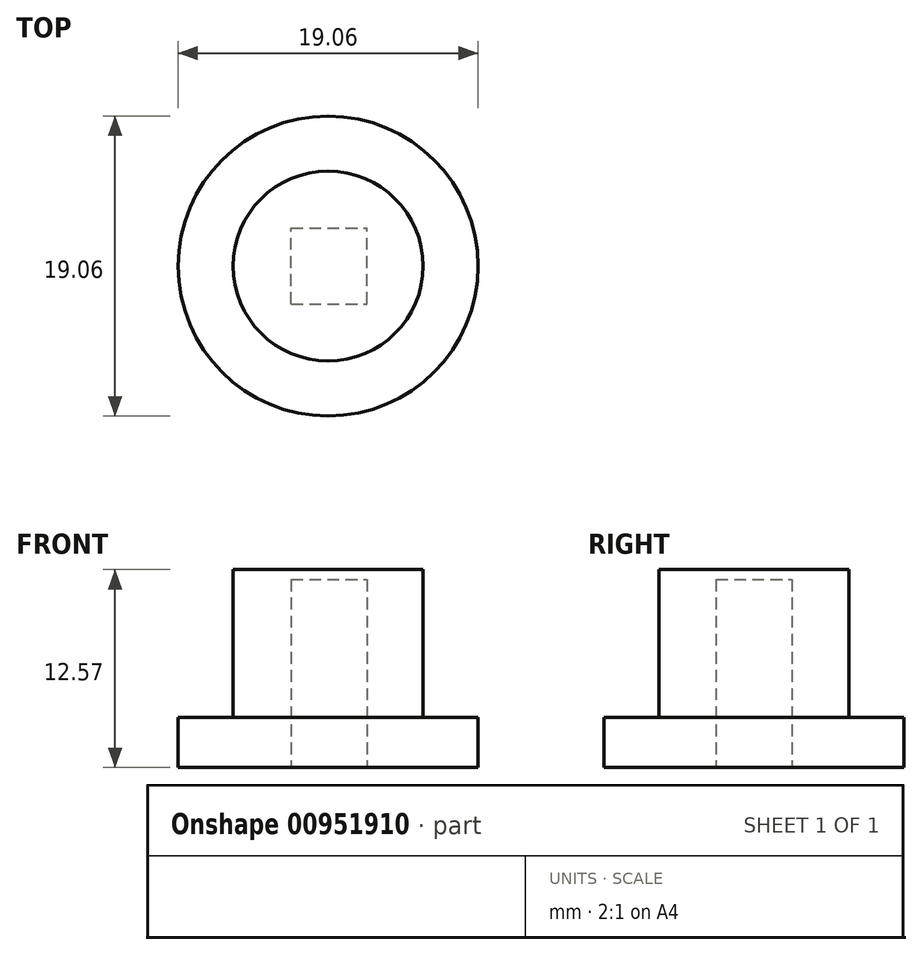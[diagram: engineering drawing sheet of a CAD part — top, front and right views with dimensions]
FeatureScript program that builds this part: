
annotation { "Feature Type Name" : "Feature", "Feature Type Description" : "" }
export const myFeature = defineFeature(function(context is Context, id is Id, definition is map)
    precondition{}
    {
        {
            var Q0;
            Q0=qCreatedBy(makeId("Top.planeOp"),FACE);
            var sketch = newSketch(context, id + "F0", { "sketchPlane" : qUnion([Q0])});
            skCircle(sketch, "E0", {"center": v(0, 0) * mm, "radius": 9.53 * mm});
            skSolve(sketch);
        }
        {
            var Q0;
            Q0=makeQuery(id+"F0.imprint","IMPRINT",FACE,{"disambiguationData":[TD([[makeQuery(id+"F0.imprint","IMPRINT",EDGE,{"derivedFrom":sQuery(id+"F0.wireOp",EDGE,"E0")}),1.0]])]});
            extrude(context, id + "F1", {"entities" : qUnion([Q0]), "depth" : 3.17 * mm, "offsetDistance" : 25.4 * mm});
        }
        {
            var Q0;
            Q0=makeQuery(id+"F1.opExtrude","CAP_FACE",FACE,{"disambiguationData":[OSD([sQuery(id+"F0.wireOp",EDGE,"E0")])],"isStart":false});
            var sketch = newSketch(context, id + "F2", { "sketchPlane" : qUnion([Q0])});
            skCircle(sketch, "E1", {"center": v(0, 0) * mm, "radius": 6.03 * mm});
            skSolve(sketch);
        }
        {
            var Q0;
            Q0=makeQuery(id+"F2.imprint","IMPRINT",FACE,{"disambiguationData":[TD([[makeQuery(id+"F2.imprint","IMPRINT",EDGE,{"derivedFrom":sQuery(id+"F2.wireOp",EDGE,"E1")}),1.0]])]});
            extrude(context, id + "F3", {"entities" : qUnion([Q0]), "operationType" : NewBodyOperationType.ADD, "depth" : 9.4 * mm, "offsetDistance" : 25.4 * mm});
        }
        {
            var Q0;
            Q0=makeQuery(id+"F1.opExtrude","CAP_FACE",FACE,{"disambiguationData":[OSD([sQuery(id+"F0.wireOp",EDGE,"E0")])],"isStart":true});
            var sketch = newSketch(context, id + "F4", { "sketchPlane" : qUnion([Q0])});
            skLineSegment(sketch, "E2.bottom", {"start": v(-2.34, 2.41) * mm, "end": v(2.48, 2.41) * mm});
            skLineSegment(sketch, "E2.top", {"start": v(-2.34, -2.41) * mm, "end": v(2.48, -2.41) * mm});
            skLineSegment(sketch, "E2.left", {"start": v(-2.34, 2.41) * mm, "end": v(-2.34, -2.41) * mm});
            skLineSegment(sketch, "E2.right", {"start": v(2.48, 2.41) * mm, "end": v(2.48, -2.41) * mm});
            skSolve(sketch);
        }
        {
            var Q0;
            Q0=makeQuery(id+"F4.imprint","IMPRINT",FACE,{"disambiguationData":[TD([[makeQuery(id+"F4.imprint","IMPRINT",EDGE,{"derivedFrom":sQuery(id+"F4.wireOp",EDGE,"E2.bottom")}),-1.0]])]});
            extrude(context, id + "F5", {"entities" : qUnion([Q0]), "operationType" : NewBodyOperationType.REMOVE, "oppositeDirection" : true, "depth" : 11.94 * mm, "offsetDistance" : 25.4 * mm});
        }
    });
